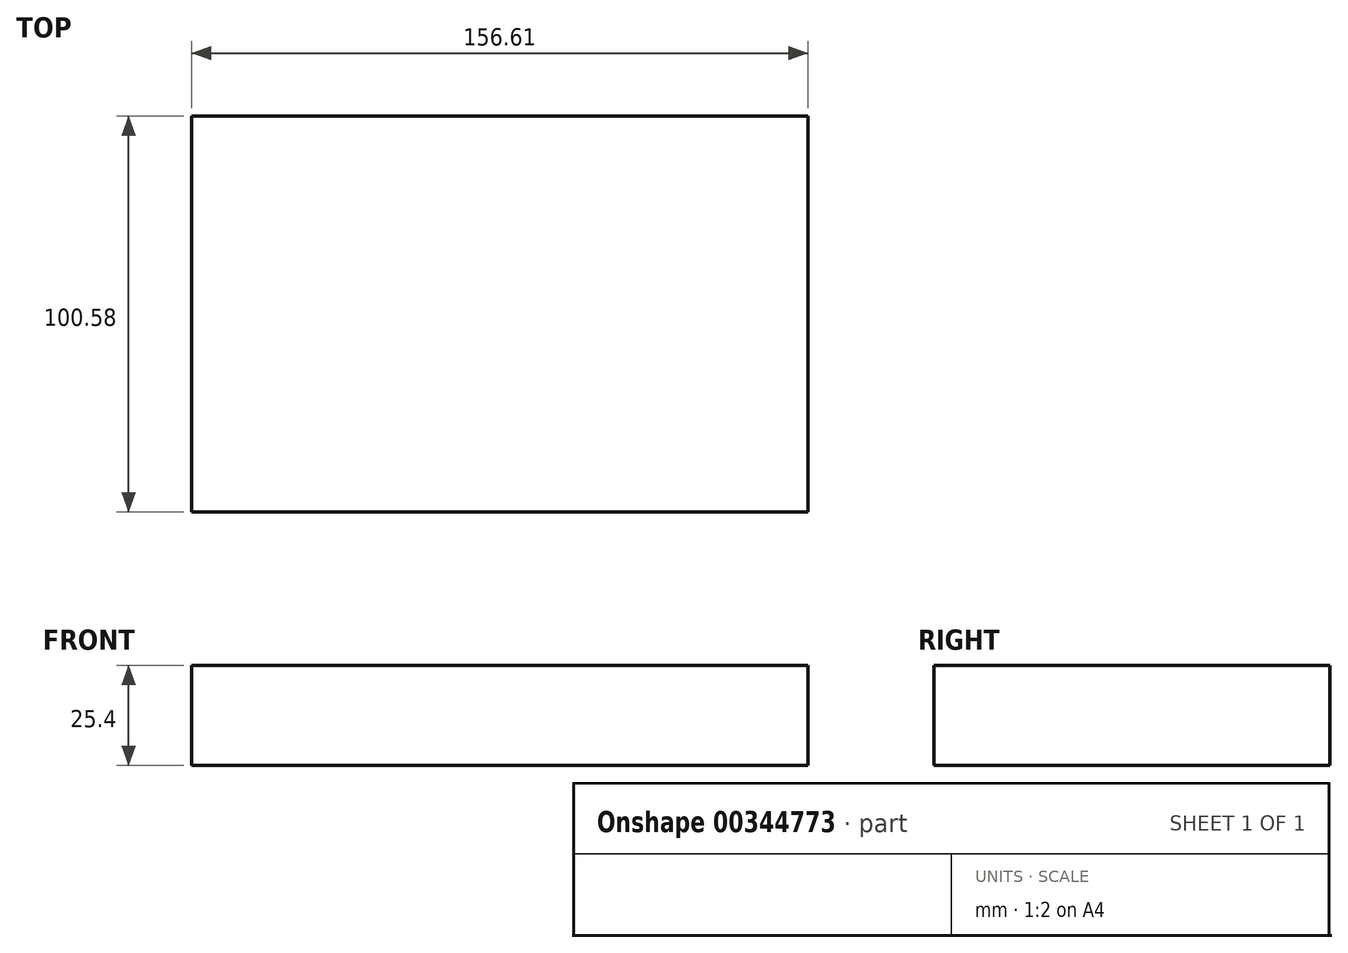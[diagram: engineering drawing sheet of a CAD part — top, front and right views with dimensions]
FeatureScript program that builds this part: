
annotation { "Feature Type Name" : "Feature", "Feature Type Description" : "" }
export const myFeature = defineFeature(function(context is Context, id is Id, definition is map)
    precondition{}
    {
        {
            var Q0;
            Q0=qCreatedBy(makeId("Top.planeOp"),FACE);
            var sketch = newSketch(context, id + "F0", { "sketchPlane" : qUnion([Q0])});
            skLineSegment(sketch, "E0.bottom", {"start": v(83.37, 49.83) * mm, "end": v(-73.24, 49.83) * mm});
            skLineSegment(sketch, "E0.top", {"start": v(83.37, -50.75) * mm, "end": v(-73.24, -50.75) * mm});
            skLineSegment(sketch, "E0.left", {"start": v(83.37, 49.83) * mm, "end": v(83.37, -50.75) * mm});
            skLineSegment(sketch, "E0.right", {"start": v(-73.24, 49.83) * mm, "end": v(-73.24, -50.75) * mm});
            skPoint(sketch, "E0.middle", {"position": v(5.06, -0.46) * mm});
            skSolve(sketch);
        }
        {
            var Q0;
            Q0=makeQuery(id+"F0.imprint","IMPRINT",FACE,{"disambiguationData":[TD([[makeQuery(id+"F0.imprint","IMPRINT",EDGE,{"derivedFrom":sQuery(id+"F0.wireOp",EDGE,"E0.bottom")}),1.0]])]});
            extrude(context, id + "F1", {"entities" : qUnion([Q0]), "depth" : 25.4 * mm});
        }
    });
